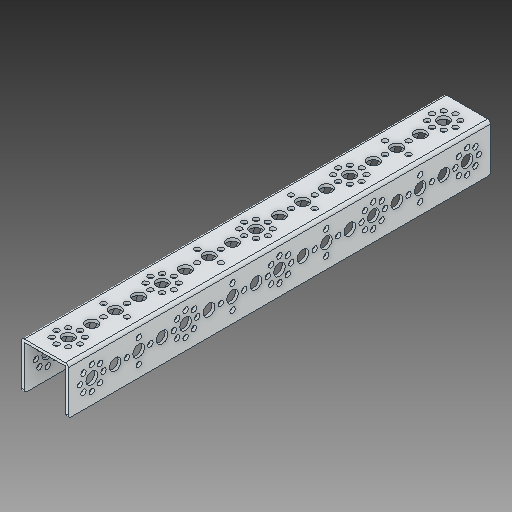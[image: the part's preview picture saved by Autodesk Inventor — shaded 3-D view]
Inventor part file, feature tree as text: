
AUTODESK INVENTOR PART (.ipt)
format: ipt  version: 2018 (Build 220112000, 112)  size: 388,608 bytes
history: native  units: in
note: dims shown in document units (in); Inventor stores cm internally (conversion verified against a paired STEP export)
features: fillet x1
ambient origin geometry x8: Origin, YZ Plane, XZ Plane, XY Plane, X Axis, Y Axis, Z Axis, Center Point
bodies: Solid1 (feature_tree)
feature tree (1):
  fillet  "Fillet1"  [1 undecoded]
note: 1 required parameter value undecoded (feature->parameter linkage not recoverable at this tier; creation-order binding heuristic only, values carry confidence <= 0.55)
